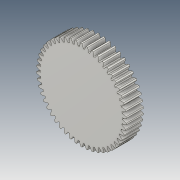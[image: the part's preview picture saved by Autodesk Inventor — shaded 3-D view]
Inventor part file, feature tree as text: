
AUTODESK INVENTOR PART (.ipt)
format: ipt  version: 2021 (Build 250183000, 183)  size: 333,312 bytes
history: native  units: mm (DEFAULTED — no unit token found)
features: plane x3, other x3, sketch x2, extrude x1
ambient origin geometry x8: Origin, YZ Plane, XZ Plane, XY Plane, X Axis, Y Axis, Z Axis, Center Point
bodies: Solid1 (feature_tree)
feature tree (9):
  extrude  "Extrusion1"  Depth=25.4mm TaperAngle=0.0deg
  plane  "Work Plane1"
  plane  "Work Plane2"
  plane  "Work Plane3"
  other  "Engrenagem reta"
  sketch  "Sketch1"  dims[d0=132.08mm d1=25.4mm d2=0.0mm]
  sketch  "Sketch2"  dims[d3=127.0mm d4=76.2mm d5=0.0mm d6=0.0mm d7=0.628319mm d9=0.0mm d14=0.0mm d15=135.89mm d16=0.0mm d17=0.0mm d18=0.0mm d19=135.89mm]
  other  "Srf1"
  other  "Diâmetro do flanco"
